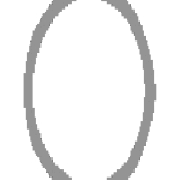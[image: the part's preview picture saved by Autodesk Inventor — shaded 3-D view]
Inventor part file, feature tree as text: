
AUTODESK INVENTOR PART (.ipt)
format: ipt  version: 2021 (Build 250183000, 183)  size: 112,128 bytes
history: native  units: in
note: dims shown in document units (in); Inventor stores cm internally (conversion verified against a paired STEP export)
features: other x4, sketch x3, plane x1
ambient origin geometry x8: Origin, YZ Plane, XZ Plane, XY Plane, X Axis, Y Axis, Z Axis, Center Point
bodies: Solid1 (feature_tree), Body (feature_tree)
feature tree (8):
  other  "Driven Length"
  other  "Frame Generator"
  other  "Start Plane"
  other  "End Plane"
  sketch  "Sketch"  dims[d2=15.625in d4=-0.0in d5=15.625in d6=0.12in d7=0.0in d8=90.0deg d9=15.625in]
  sketch  "Sketch2"  dims[d0=1.0in]
  plane  "Work Plane3"
  sketch  "Sketch3"  dims[d1=0.065in]
